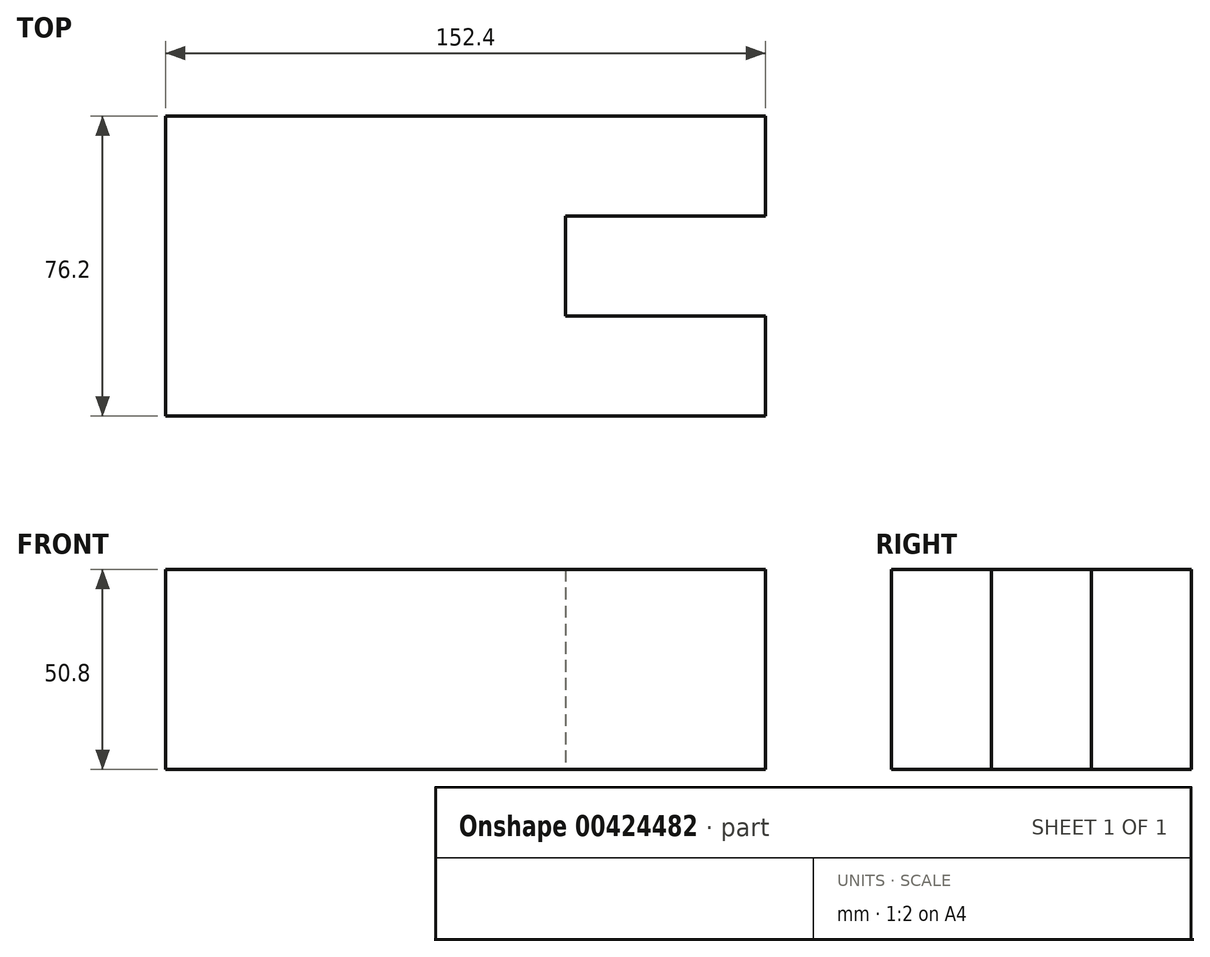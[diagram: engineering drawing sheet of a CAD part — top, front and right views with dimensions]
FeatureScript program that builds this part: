
annotation { "Feature Type Name" : "Feature", "Feature Type Description" : "" }
export const myFeature = defineFeature(function(context is Context, id is Id, definition is map)
    precondition{}
    {
        {
            var Q0;
            Q0=qCreatedBy(makeId("Top.planeOp"),FACE);
            var sketch = newSketch(context, id + "F0", { "sketchPlane" : qUnion([Q0])});
            skLineSegment(sketch, "E0", {"start": v(0, 0) * mm, "end": v(0, 76.2) * mm});
            skLineSegment(sketch, "E1", {"start": v(0, 0) * mm, "end": v(152.4, 0) * mm});
            skLineSegment(sketch, "E2", {"start": v(0, 76.2) * mm, "end": v(152.4, 76.2) * mm});
            skLineSegment(sketch, "E3", {"start": v(152.4, 76.2) * mm, "end": v(152.4, 50.8) * mm});
            skLineSegment(sketch, "E4", {"start": v(152.4, 50.8) * mm, "end": v(101.6, 50.8) * mm});
            skLineSegment(sketch, "E5", {"start": v(101.6, 50.8) * mm, "end": v(101.6, 25.4) * mm});
            skLineSegment(sketch, "E6", {"start": v(101.6, 25.4) * mm, "end": v(152.4, 25.4) * mm});
            skLineSegment(sketch, "E7", {"start": v(152.4, 25.4) * mm, "end": v(152.4, 0) * mm});
            skSolve(sketch);
        }
        {
            var Q0;
            Q0=makeQuery(id+"F0.imprint","IMPRINT",FACE,{"disambiguationData":[TD([[makeQuery(id+"F0.imprint","IMPRINT",EDGE,{"derivedFrom":sQuery(id+"F0.wireOp",EDGE,"E0")}),-1.0]])]});
            extrude(context, id + "F1", {"entities" : qUnion([Q0]), "depth" : 50.8 * mm});
        }
    });
